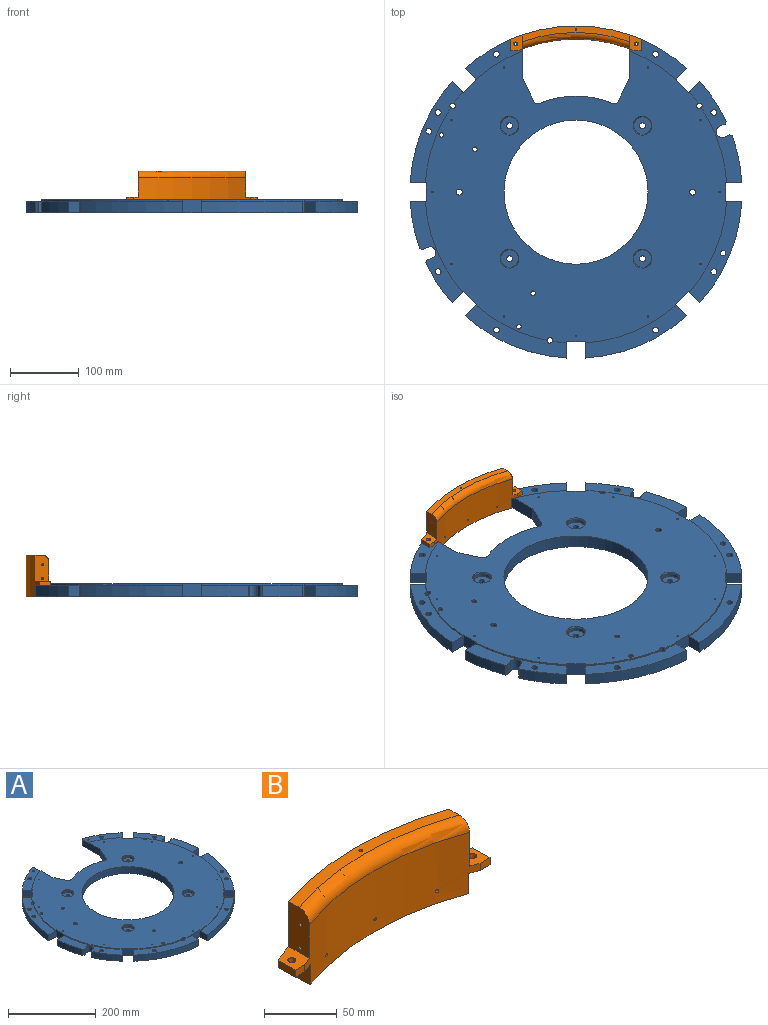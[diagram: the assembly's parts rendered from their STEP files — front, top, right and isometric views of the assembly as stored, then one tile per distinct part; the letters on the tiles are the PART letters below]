
ASSEMBLY  parts=2 mates=1
PART A: 134 faces, bbox 483.2x470x19.1 mm
  f0: cylinder r=220mm len=20.8mm, axis (0,0,1), area 42.9mm2, adj f6,f21,f66,f133
  f1: cylinder r=220mm len=16.31mm, axis (0,0,1), area 42.9mm2, adj f6,f17,f60,f132
  f2: cylinder r=220mm len=109.42mm, axis (0,0,1), area 239.7mm2, adj f6,f25,f64,f131
  f3: cylinder r=242mm len=68.77mm, axis (0,0,-1), area 1197.3mm2, adj f14,f38,f42,f60
  f4: cylinder r=242mm len=58.47mm, axis (0,0,-1), area 1195.8mm2, adj f23,f36,f42,f62
  f5: cylinder r=242mm len=80.68mm, axis (0,0,-1), area 1604.1mm2, adj f27,f41,f42,f56
  f6: plane 439.17x425.29mm, normal (0,0,1), area 102290.3mm2, adj f0,f1,f2,f14,f15,f16,f17,f18
  f7: cylinder r=242mm len=147.81mm, axis (0,0,-1), area 2771.9mm2, adj f25,f26,f42,f64
  f8: cylinder r=242mm len=68.77mm, axis (0,0,-1), area 1197.3mm2, adj f24,f37,f42,f62
  f9: cylinder r=242mm len=147.81mm, axis (0,0,-1), area 2771.9mm2, adj f21,f22,f42,f66
  f10: cylinder r=242mm len=147.81mm, axis (0,0,-1), area 2771.9mm2, adj f19,f20,f42,f68
  f11: cylinder r=242mm len=147.81mm, axis (0,0,-1), area 2771.9mm2, adj f15,f18,f42,f71
  f12: cylinder r=242mm len=81.23mm, axis (0,0,-1), area 1614mm2, adj f16,f40,f42,f58
  f13: cylinder r=242mm len=58.47mm, axis (0,0,-1), area 1195.8mm2, adj f17,f39,f42,f60
  f14: plane 23.62x19.05mm, normal (0,-1,0), area 404.8mm2, adj f3,f6,f42,f44,f60,f61
  f15: plane 23.62x19.05mm, normal (0,1,0), area 404.8mm2, adj f6,f11,f42,f44,f70,f71
  f16: plane 19.05x16.7mm, normal (0.71,-0.71,0), area 404.8mm2, adj f6,f12,f42,f45,f58,f59
  f17: plane 19.05x16.7mm, normal (-0.71,0.71,0), area 404.8mm2, adj f1,f6,f13,f42,f45,f60
  f18: plane 19.05x16.7mm, normal (-0.71,-0.71,0), area 404.8mm2, adj f6,f11,f42,f46,f70,f71
  f19: plane 19.05x16.7mm, normal (0.71,0.71,0), area 404.8mm2, adj f6,f10,f42,f46,f68,f69
  f20: plane 23.62x19.05mm, normal (-1,0,0), area 404.8mm2, adj f6,f10,f42,f47,f68,f69
  f21: plane 23.62x19.05mm, normal (1,0,0), area 404.8mm2, adj f0,f6,f9,f42,f47,f66
  f22: plane 19.05x16.7mm, normal (-0.71,0.71,0), area 404.8mm2, adj f6,f9,f42,f48,f66,f67
  f23: plane 19.05x16.7mm, normal (0.71,-0.71,0), area 404.8mm2, adj f4,f6,f42,f48,f62,f63
  f24: plane 23.62x19.05mm, normal (0,1,0), area 404.8mm2, adj f6,f8,f42,f49,f62,f63
  f25: plane 23.62x19.05mm, normal (0,-1,0), area 404.8mm2, adj f2,f6,f7,f42,f49,f64
  f26: plane 19.05x16.7mm, normal (0.71,0.71,0), area 404.8mm2, adj f6,f7,f42,f50,f64,f65
  f27: plane 19.05x16.7mm, normal (-0.71,-0.71,0), area 404.8mm2, adj f5,f6,f42,f50,f56,f57
  f28: plane 59.61x19.05mm, normal (1,0,0), area 1092.1mm2, adj f6,f41,f42,f52,f56,f57
  f29: plane 59.01x19.05mm, normal (-1,0,0), area 1082mm2, adj f6,f40,f42,f53,f58,f59
  f30: cylinder r=8.4mm len=17mm, axis (0,0,1), area 448.6mm2, adj f31,f32,f42,f62
  f31: plane 17x8.45mm, normal (-0.38,0.92,0), area 155.5mm2, adj f30,f36,f42,f62
  f32: plane 17x8.37mm, normal (0.38,-0.92,0), area 153.9mm2, adj f30,f37,f42,f62
  f33: plane 17x8.37mm, normal (-0.38,0.92,0), area 153.9mm2, adj f34,f38,f42,f60
  f34: cylinder r=8.4mm len=17mm, axis (0,0,1), area 448.6mm2, adj f33,f35,f42,f60
  f35: plane 17x8.45mm, normal (0.38,-0.92,0), area 155.5mm2, adj f34,f39,f42,f60
  f36: plane 17x3.56mm, normal (-0.94,0.35,0), area 64.7mm2, adj f4,f31,f42,f62
  f37: plane 17x3.52mm, normal (-0.38,-0.92,0), area 64.7mm2, adj f8,f32,f42,f62
  f38: plane 17x3.52mm, normal (0.38,0.92,0), area 64.7mm2, adj f3,f33,f42,f60
  f39: plane 17x3.56mm, normal (0.94,-0.35,0), area 64.7mm2, adj f13,f35,f42,f60
  f40: plane 17x2.08mm, normal (-0.71,0.71,0), area 50mm2, adj f12,f29,f42,f58
  f41: plane 17x2.63mm, normal (0.44,0.9,0), area 49.8mm2, adj f5,f28,f42,f56
  f42: plane 483.25x469.99mm, normal (0,0,-1), area 127465.8mm2, adj f3,f4,f5,f7,f8,f9,f10,f11
  f43: cylinder r=105mm len=210mm, axis (0,0,-1), area 12567.9mm2, adj f6,f42
  f44: plane 27x19.05mm, normal (1,0,0), area 514.3mm2, adj f6,f14,f15,f42
  f45: plane 19.09x19.09mm, normal (0.71,0.71,0), area 514.3mm2, adj f6,f16,f17,f42
  f46: plane 19.09x19.09mm, normal (0.71,-0.71,0), area 514.3mm2, adj f6,f18,f19,f42
  f47: plane 27x19.05mm, normal (0,-1,0), area 514.3mm2, adj f6,f20,f21,f42
  f48: plane 19.09x19.09mm, normal (-0.71,-0.71,0), area 514.3mm2, adj f6,f22,f23,f42
  f49: plane 27x19.05mm, normal (-1,0,0), area 514.3mm2, adj f6,f24,f25,f42
  f50: plane 19.09x19.09mm, normal (-0.71,0.71,0), area 514.3mm2, adj f6,f26,f27,f42
  f51: cylinder r=6.35mm len=19.05mm, axis (0,0,1), area 184.8mm2, adj f6,f42,f52,f55
  f52: plane 34.76x19.05mm, normal (0.91,0.42,0), area 730.6mm2, adj f6,f28,f42,f51
  f53: plane 34.76x19.05mm, normal (-0.91,0.42,0), area 730.6mm2, adj f6,f29,f42,f54
  f54: cylinder r=6.35mm len=19.05mm, axis (0,0,1), area 184.8mm2, adj f6,f42,f53,f55
  f55: cylinder r=140mm len=107.21mm, axis (0,0,1), area 2095.9mm2, adj f6,f42,f51,f54
  f56: plane 83.31x63.36mm, normal (0,0,1), area 1868.9mm2, adj f5,f27,f28,f41,f57,f95,f108
  f57: cylinder r=220mm len=67.72mm, axis (0,0,1), area 163.1mm2, adj f6,f27,f28,f56
  f58: plane 83.31x63.55mm, normal (0,0,1), area 1868.9mm2, adj f12,f16,f29,f40,f59,f94,f107
  f59: cylinder r=220mm len=67.72mm, axis (0,0,1), area 163.1mm2, adj f6,f16,f29,f58
  f60: plane 147.81x76.81mm, normal (0,0,1), area 2999.4mm2, adj f1,f3,f13,f14,f17,f33,f34,f35
  f61: cylinder r=220mm len=109.42mm, axis (0,0,1), area 239.7mm2, adj f6,f14,f60,f132
  f62: plane 147.81x76.81mm, normal (0,0,1), area 3019.8mm2, adj f4,f8,f23,f24,f30,f31,f32,f36
  f63: cylinder r=220mm len=132.22mm, axis (0,0,1), area 298.8mm2, adj f6,f23,f24,f62
  f64: plane 147.81x76.81mm, normal (0,0,1), area 3258.9mm2, adj f2,f7,f25,f26,f65,f96,f103,f104
  f65: cylinder r=220mm len=16.31mm, axis (0,0,1), area 42.9mm2, adj f6,f26,f64,f131
  f66: plane 147.81x76.81mm, normal (0,0,1), area 3318.5mm2, adj f0,f9,f21,f22,f67,f98,f133
  f67: cylinder r=220mm len=103.63mm, axis (0,0,1), area 239.7mm2, adj f6,f22,f66,f133
  f68: plane 147.81x76.81mm, normal (0,0,1), area 3339mm2, adj f10,f19,f20,f69,f99
  f69: cylinder r=220mm len=132.22mm, axis (0,0,1), area 298.8mm2, adj f6,f19,f20,f68
  f70: cylinder r=220mm len=132.22mm, axis (0,0,1), area 298.8mm2, adj f6,f15,f18,f71
  f71: plane 147.81x76.81mm, normal (0,0,1), area 3287.4mm2, adj f11,f15,f18,f70,f100,f102
  f72: cylinder r=4.3mm len=12mm, axis (0,0,1), area 324.2mm2, adj f42,f73
  f73: plane 25.6x25.6mm, normal (0,0,1), area 456.6mm2, adj f72,f74
  f74: cylinder r=12.8mm len=25.6mm, axis (0,0,1), area 406.1mm2, adj f73,f87
  f75: cylinder r=4.3mm len=12mm, axis (0,0,1), area 324.2mm2, adj f42,f76
  f76: plane 25.6x25.6mm, normal (0,0,1), area 456.6mm2, adj f75,f77
  f77: cylinder r=12.8mm len=25.6mm, axis (0,0,1), area 406.1mm2, adj f76,f84
  f78: cylinder r=4.3mm len=12mm, axis (0,0,1), area 324.2mm2, adj f42,f79
  f79: plane 25.6x25.6mm, normal (0,0,1), area 456.6mm2, adj f78,f80
  f80: cylinder r=12.8mm len=25.6mm, axis (0,0,1), area 406.1mm2, adj f79,f85
  f81: cylinder r=4.3mm len=12mm, axis (0,0,1), area 324.2mm2, adj f42,f82
  f82: plane 25.6x25.6mm, normal (0,0,1), area 456.6mm2, adj f81,f83
  f83: cylinder r=12.8mm len=25.6mm, axis (0,0,1), area 406.1mm2, adj f82,f86
  f84: cone r=12.8mm half-angle=26.6deg, axis (0,0,1), area 186.9mm2, adj f6,f77
  f85: cone r=12.8mm half-angle=26.6deg, axis (0,0,1), area 186.9mm2, adj f6,f80
  f86: cone r=12.8mm half-angle=26.6deg, axis (0,0,1), area 186.9mm2, adj f6,f83
  f87: cone r=12.8mm half-angle=26.6deg, axis (0,0,1), area 186.9mm2, adj f6,f74
  f88: cylinder r=4.4mm len=19.05mm, axis (0,0,1), area 526.7mm2, adj f6,f42
  f89: cylinder r=4.4mm len=19.05mm, axis (0,0,1), area 526.7mm2, adj f6,f42
  f90: cylinder r=3.4mm len=19.05mm, axis (0,0,1), area 407mm2, adj f6,f42
  f91: cylinder r=3.4mm len=19.05mm, axis (0,0,1), area 407mm2, adj f6,f42
  f92: cylinder r=3.4mm len=19.05mm, axis (0,0,1), area 407mm2, adj f6,f42
  f93: cylinder r=3.4mm len=19.05mm, axis (0,0,1), area 407mm2, adj f6,f42
  f94: cylinder r=4.3mm len=17mm, axis (0,0,1), area 459.3mm2, adj f42,f58
  f95: cylinder r=4.3mm len=17mm, axis (0,0,1), area 459.3mm2, adj f42,f56
  f96: cylinder r=4.3mm len=17mm, axis (0,0,1), area 459.3mm2, adj f42,f64
  f97: cylinder r=4.3mm len=17mm, axis (0,0,1), area 459.3mm2, adj f42,f62
  f98: cylinder r=4.3mm len=17mm, axis (0,0,1), area 459.3mm2, adj f42,f66
  f99: cylinder r=4.3mm len=17mm, axis (0,0,1), area 459.3mm2, adj f42,f68
  f100: cylinder r=4.3mm len=17mm, axis (0,0,1), area 459.3mm2, adj f42,f71
  f101: cylinder r=4.3mm len=17mm, axis (0,0,1), area 459.3mm2, adj f42,f60
  f102: cylinder r=4.05mm len=17mm, axis (0,0,1), area 432.6mm2, adj f42,f71
  f103: cylinder r=4.05mm len=17mm, axis (0,0,1), area 216.3mm2, adj f42,f64,f105,f106
  f104: cylinder r=4.05mm len=17mm, axis (0,0,1), area 216.3mm2, adj f42,f64,f105,f106
  f105: plane 17x0.92mm, normal (-0.38,-0.92,0), area 17mm2, adj f42,f64,f103,f104
  f106: plane 17x0.92mm, normal (0.38,0.92,0), area 17mm2, adj f42,f64,f103,f104
  f107: cylinder r=2.1mm len=17mm, axis (0,0,1), area 224.3mm2, adj f42,f58
  f108: cylinder r=2.1mm len=17mm, axis (0,0,1), area 224.3mm2, adj f42,f56
  f109: cone r=1.25mm half-angle=59deg, axis (0,0,1), area 5.7mm2, adj f110
  f110: cylinder r=1.25mm len=8.5mm, axis (0,0,1), area 66.8mm2, adj f6,f109
  f111: cone r=1.25mm half-angle=59deg, axis (0,0,1), area 5.7mm2, adj f112
  f112: cylinder r=1.25mm len=8.5mm, axis (0,0,1), area 66.8mm2, adj f6,f111
  f113: cone r=1.25mm half-angle=59deg, axis (0,0,1), area 5.7mm2, adj f114
  f114: cylinder r=1.25mm len=8.5mm, axis (0,0,1), area 66.8mm2, adj f6,f113
  f115: cone r=1.25mm half-angle=59deg, axis (0,0,1), area 5.7mm2, adj f116
  f116: cylinder r=1.25mm len=8.5mm, axis (0,0,1), area 66.8mm2, adj f6,f115
  f117: cone r=1.25mm half-angle=59deg, axis (0,0,1), area 5.7mm2, adj f118
  f118: cylinder r=1.25mm len=8.5mm, axis (0,0,1), area 66.8mm2, adj f6,f117
  f119: cone r=1.25mm half-angle=59deg, axis (0,0,1), area 5.7mm2, adj f120
  f120: cylinder r=1.25mm len=8.5mm, axis (0,0,1), area 66.8mm2, adj f6,f119
  f121: cone r=1.25mm half-angle=59deg, axis (0,0,1), area 5.7mm2, adj f122
  f122: cylinder r=1.25mm len=8.5mm, axis (0,0,1), area 66.8mm2, adj f6,f121
  f123: cone r=1.25mm half-angle=59deg, axis (0,0,1), area 5.7mm2, adj f124
  f124: cylinder r=1.25mm len=8.5mm, axis (0,0,1), area 66.8mm2, adj f6,f123
  f125: cone r=1.25mm half-angle=59deg, axis (0,0,1), area 5.7mm2, adj f126
  f126: cylinder r=1.25mm len=8.5mm, axis (0,0,1), area 66.8mm2, adj f6,f125
  f127: cone r=1.25mm half-angle=59deg, axis (0,0,1), area 5.7mm2, adj f128
  f128: cylinder r=1.25mm len=8.5mm, axis (0,0,1), area 66.8mm2, adj f6,f127
  f129: cone r=1.25mm half-angle=59deg, axis (0,0,1), area 5.7mm2, adj f130
  f130: cylinder r=1.25mm len=8.5mm, axis (0,0,1), area 66.8mm2, adj f6,f129
  f131: cylinder r=4mm len=19.05mm, axis (0,0,1), area 455.3mm2, adj f2,f6,f42,f64,f65
  f132: cylinder r=4mm len=19.05mm, axis (0,0,1), area 455.3mm2, adj f1,f6,f42,f60,f61
  f133: cylinder r=4mm len=19.05mm, axis (0,0,1), area 455.3mm2, adj f0,f6,f42,f66,f67
PART B: 35 faces, bbox 190x53x61 mm
  f0: cylinder r=223mm len=170.8mm, axis (0,0,-1), area 8248mm2, adj f2,f3,f4,f7,f8,f9,f10,f12
  f1: cylinder r=242mm len=190mm, axis (0,0,-1), area 9871.6mm2, adj f2,f3,f4,f5,f6,f8,f9,f11
  f2: plane 154x32.72mm, normal (0,0,-1), area 2982.4mm2, adj f0,f1,f14,f15
  f3: plane 38x20.17mm, normal (1,0,0), area 735.9mm2, adj f0,f1,f5,f12,f25,f27,f34
  f4: plane 38x20.17mm, normal (-1,0,0), area 735.9mm2, adj f0,f1,f5,f8,f21,f23,f34
  f5: plane 156x22.95mm, normal (0,0,1), area 1501.2mm2, adj f1,f3,f4,f19,f34
  f6: plane 16.57x6mm, normal (-1,0,0), area 99.4mm2, adj f1,f7,f8,f9
  f7: plane 9.6x6mm, normal (0,-1,0), area 57.6mm2, adj f0,f6,f8,f9
  f8: plane 23.09x17mm, normal (0,0,1), area 303.6mm2, adj f0,f1,f4,f6,f7,f17
  f9: plane 23.42x18mm, normal (0,0,-1), area 323.7mm2, adj f0,f1,f6,f7,f14,f17
  f10: plane 9.6x6mm, normal (0,-1,0), area 57.6mm2, adj f0,f11,f12,f13
  f11: plane 16.57x6mm, normal (1,0,0), area 99.4mm2, adj f1,f10,f12,f13
  f12: plane 23.09x17mm, normal (0,0,1), area 303.6mm2, adj f0,f1,f3,f10,f11,f16
  f13: plane 23.42x18mm, normal (0,0,-1), area 323.7mm2, adj f0,f1,f10,f11,f15,f16
  f14: plane 20.14x17mm, normal (-1,0,0), area 342.4mm2, adj f0,f1,f2,f9
  f15: plane 20.14x17mm, normal (1,0,0), area 342.4mm2, adj f0,f1,f2,f13
  f16: cylinder r=2.8mm len=6mm, axis (0,0,-1), area 105.6mm2, adj f12,f13
  f17: cylinder r=2.8mm len=6mm, axis (0,0,-1), area 105.6mm2, adj f8,f9
  f18: cone r=1.25mm half-angle=59deg, axis (0,0,1), area 5.7mm2, adj f19
  f19: cylinder r=1.25mm len=8.5mm, axis (0,0,1), area 66.8mm2, adj f5,f18
  f20: cone r=1.25mm half-angle=59deg, axis (-1,0,0), area 5.7mm2, adj f21
  f21: cylinder r=1.25mm len=7.5mm, axis (-1,0,0), area 58.9mm2, adj f4,f20
  f22: cone r=1.25mm half-angle=59deg, axis (-1,0,0), area 5.7mm2, adj f23
  f23: cylinder r=1.25mm len=7.5mm, axis (-1,0,0), area 58.9mm2, adj f4,f22
  f24: cone r=1.25mm half-angle=59deg, axis (1,0,0), area 5.7mm2, adj f25
  f25: cylinder r=1.25mm len=7.5mm, axis (1,0,0), area 58.9mm2, adj f3,f24
  f26: cone r=1.25mm half-angle=59deg, axis (1,0,0), area 5.7mm2, adj f27
  f27: cylinder r=1.25mm len=7.5mm, axis (1,0,0), area 58.9mm2, adj f3,f26
  f28: cylinder r=1.25mm len=8.9mm, axis (0,-1,0), area 69.9mm2, adj f0,f29
  f29: cone r=1.25mm half-angle=59deg, axis (0,-1,0), area 5.7mm2, adj f28
  f30: cylinder r=1.25mm len=9.24mm, axis (-0.24,-0.97,0), area 69.9mm2, adj f0,f31
  f31: cone r=1.25mm half-angle=59deg, axis (-0.24,-0.97,0), area 5.7mm2, adj f30
  f32: cylinder r=1.25mm len=9.24mm, axis (0.24,-0.97,0), area 69.9mm2, adj f0,f33
  f33: cone r=1.25mm half-angle=59deg, axis (0.24,-0.97,0), area 5.7mm2, adj f32
  f34: torus R=232.53mm, axis (0,0,-1), area 2382.9mm2, adj f0,f3,f4,f5
PLACE A t=(-95.39,-16.59,170.63)mm
PLACE B t=(-95.39,189.41,191.6)mm
MATE fastened B.f17 <-> A.f108  axis (0,0,-1) through (-183.39,199.41,178.1)mm
